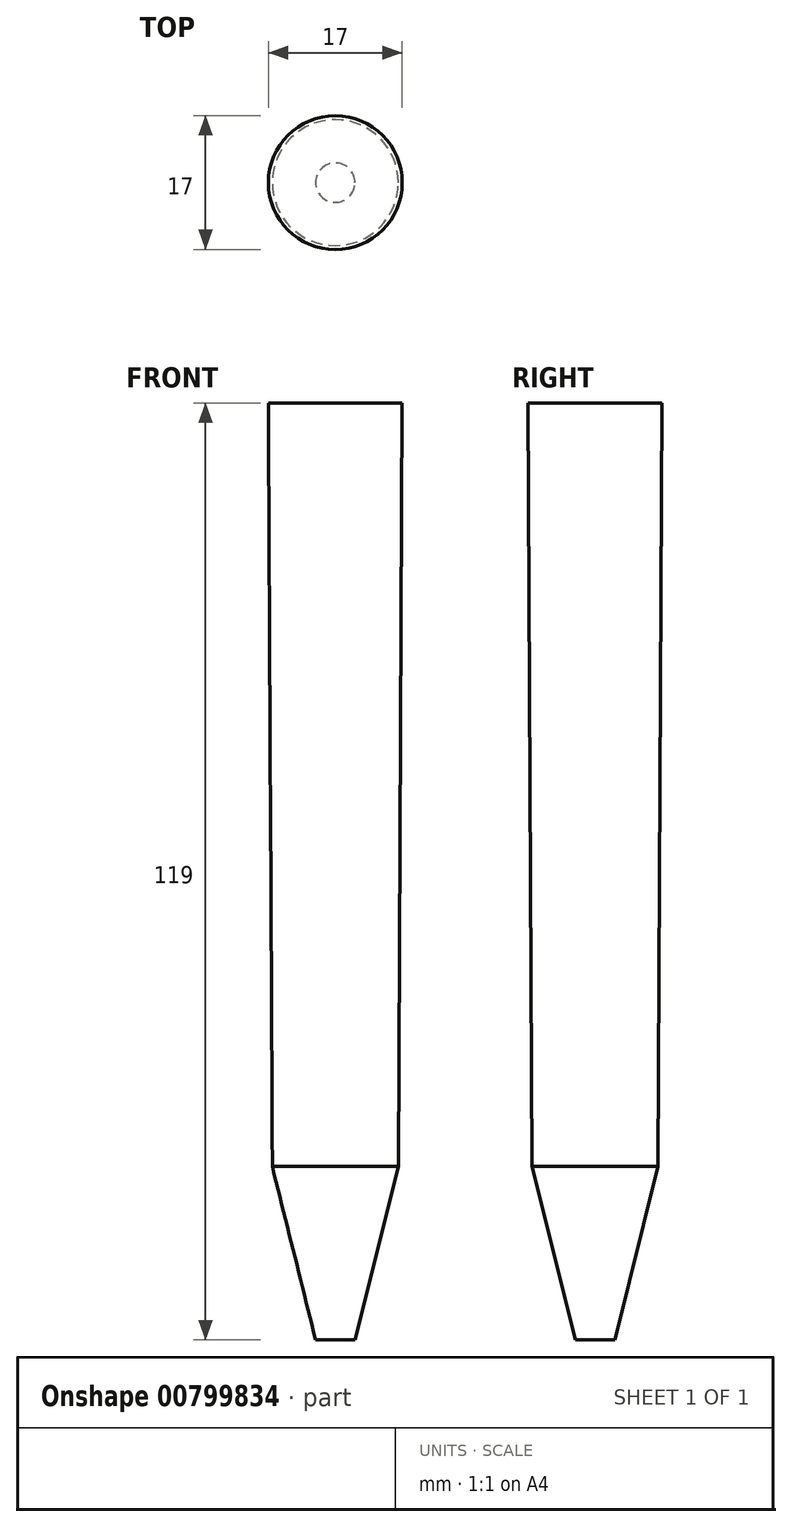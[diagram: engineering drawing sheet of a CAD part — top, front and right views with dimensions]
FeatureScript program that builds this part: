
annotation { "Feature Type Name" : "Feature", "Feature Type Description" : "" }
export const myFeature = defineFeature(function(context is Context, id is Id, definition is map)
    precondition{}
    {
        {
            var Q0;
            Q0=qCreatedBy(makeId("Front.planeOp"),FACE);
            var sketch = newSketch(context, id + "F0", { "sketchPlane" : qUnion([Q0])});
            skLineSegment(sketch, "E0", {"start": v(0, 0) * mm, "end": v(2.5, 0) * mm});
            skLineSegment(sketch, "E1", {"start": v(2.5, 0) * mm, "end": v(8, 22) * mm});
            skLineSegment(sketch, "E2", {"start": v(8, 22) * mm, "end": v(8.5, 119) * mm});
            skLineSegment(sketch, "E3", {"start": v(8.5, 119) * mm, "end": v(0, 119) * mm});
            skLineSegment(sketch, "E4", {"start": v(0, 119) * mm, "end": v(0, 0) * mm});
            skLineSegment(sketch, "E5", {"start": v(0, -33.5) * mm, "end": v(0, 122.5) * mm, "construction": true});
            skSolve(sketch);
        }
        {
            var Q0;
            Q0 = qSketchRegion(id + "F0", true);
            var Q1;
            Q1=sQuery(id+"F0.wireOp",EDGE,"E5");
            revolve(context, id + "F1", {"surfaceOperationType" : NewSurfaceOperationType.NEW, "entities" : qUnion([Q0]), "axis" : qUnion([Q1]), "revolveType" : RevolveType.FULL});
        }
    });
